# Revit family: Gripple Standard Hanger
name_source: partatom
category: Specialty Equipment
revit_build: Autodesk Revit 2017 (Build: 20160606_1515(x64)
units: mm (PartAtom-declared; Revit-internal decimal feet)

## family parameters
Always vertical = Yes
Cut with Voids When Loaded = No
Part Type = Normal
Room Calculation Point = No
Round Connector Dimension = Use Diameter
Shared = Yes
Work Plane-Based = Yes

## types (5) — shared parameters
Manufacturer = Gripple Ltd
URL = http://www.gripple.co.uk
zero-valued in all types: Default Elevation

## per-type parameters (varying)
| type | D | Gripple Length | Gripple Width | Hanger SWL (kg) | Model | T | T/2 | T/2 (-) | Wire Entry Triangle Top Distance | WireRadius |
| HF2 | 6 mm  [stored 0.019685 ft] | 45 mm  [stored 0.147638 ft] | 25 mm  [stored 0.082021 ft] | 45 kg | Standard Hanger No2 | 7 mm  [stored 0.0229659 ft] | 4 mm  [stored 0.0131234 ft] | -4 mm | 23 mm | 1 mm  [stored 0.00328084 ft] |
| HF3 | 6 mm  [stored 0.019685 ft] | 45 mm  [stored 0.147638 ft] | 25 mm  [stored 0.082021 ft] | 90 kg | Standard Hanger No3 | 7 mm  [stored 0.0229659 ft] | 4 mm  [stored 0.0131234 ft] | -4 mm | 23 mm | 2 mm  [stored 0.00656168 ft] |
| HF4 | 6 mm  [stored 0.019685 ft] | 62 mm  [stored 0.203412 ft] | 37 mm  [stored 0.121391 ft] | 225 kg | Standard Hanger No4 | 12 mm  [stored 0.0393701 ft] | 6 mm  [stored 0.019685 ft] | -6 mm  [stored -0.019685 ft] | 31 mm  [stored 0.101706 ft] | 2 mm  [stored 0.00656168 ft] |
| HF5 | 6 mm  [stored 0.019685 ft] | 105 mm  [stored 0.344488 ft] | 48 mm  [stored 0.15748 ft] | 325 kg | Standard Hanger No5 | 12 mm  [stored 0.0393701 ft] | 6 mm  [stored 0.019685 ft] | -6 mm  [stored -0.019685 ft] | 53 mm | 3 mm  [stored 0.00984252 ft] |
| HF1 | 5 mm  [stored 0.0164042 ft] | 40 mm  [stored 0.131234 ft] | 15 mm  [stored 0.0492126 ft] | 10 kg | Standard Hanger No1 | 7 mm  [stored 0.0229659 ft] | 4 mm  [stored 0.0131234 ft] | -4 mm | 20 mm  [stored 0.0656168 ft] | 1 mm  [stored 0.00328084 ft] |

note: column(s) folded — value = type name in every type: Assembly Code

note: [stored X ft] marks values corroborated as IEEE doubles in the binary element streams (Revit-internal decimal feet)

## geometry (parser evidence)
native form markers: Blend x4
no freeform markers — native parametric forms only
